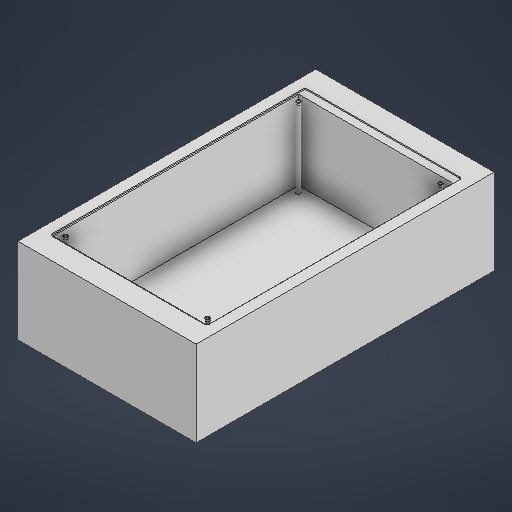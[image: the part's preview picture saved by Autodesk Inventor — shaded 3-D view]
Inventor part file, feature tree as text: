
AUTODESK INVENTOR PART (.ipt)
format: ipt  version: 2025.2 (Build 292293000, 293)  size: 246,784 bytes
history: native  units: in
note: dims shown in document units (in); Inventor stores cm internally (conversion verified against a paired STEP export)
features: extrude x6, sketch x6
ambient origin geometry x8: Origin, YZ Plane, XZ Plane, XY Plane, X Axis, Y Axis, Z Axis, Center Point
bodies: Solid1 (feature_tree)
feature tree (12):
  extrude  "Extrusion1"  Depth=10.9843in
  extrude  "Extrusion2"  Depth=5.7874in
  extrude  "Extrusion3"  Depth=0.0787in
  extrude  "Extrusion4"  Depth=0.0492in
  extrude  "Extrusion5"  Depth=5.689in
  extrude  "Extrusion6"  Depth=2.9094in TaperAngle=0.0deg
  sketch  "Sketch1"  dims[d0=6.5748in d1=10.9843in]
  sketch  "Sketch2"  dims[d2=3.1496in d3=0.0in d4=5.7874in]
  sketch  "Sketch3"  dims[d5=9.4094in d6=0.0787in]
  sketch  "Sketch4"  dims[d7=0.0433in d8=0.0in d9=0.0492in]
  sketch  "Sketch5"  dims[d10=0.0657in d11=5.689in]
  sketch  "Sketch6"  dims[d12=9.0591in d13=2.9094in d14=0.0in d15=0.1575in d16=0.2362in d17=0.2264in d18=0.1575in d19=0.2362in d20=0.2264in d21=0.1575in d22=0.2264in d23=0.2362in d24=0.1575in d25=0.2362in d26=0.2264in d27=2.9094in d28=0.0in d29=0.0984in d30=0.0984in d31=0.0984in d32=0.0984in d33=2.9094in d34=0.0in d35=0.1969in d36=0.0in d37=0.1378in d38=0.1378in d39=0.1378in d40=0.1378in d41=3.0276in d42=0.0in]
